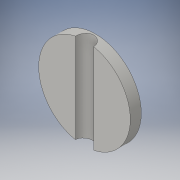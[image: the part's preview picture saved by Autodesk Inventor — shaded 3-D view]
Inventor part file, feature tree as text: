
AUTODESK INVENTOR PART (.ipt)
format: ipt  version: 2016 (Build 200138000, 138)  size: 99,840 bytes
history: native  units: in
note: dims shown in document units (in); Inventor stores cm internally (conversion verified against a paired STEP export)
features: extrude x2, sketch x2
ambient origin geometry x8: Origin, YZ Plane, XZ Plane, XY Plane, X Axis, Y Axis, Z Axis, Center Point
bodies: Solid1 (feature_tree)
feature tree (4):
  extrude  "Extrusion1"  Depth=0.06in TaperAngle=0.0deg
  extrude  "Extrusion2"  Depth=0.5in TaperAngle=0.0deg
  sketch  "Sketch1"  dims[d0=0.5in d1=0.06in d2=0.0in]
  sketch  "Sketch2"  dims[d3=0.01in d4=0.5in d5=0.0in]
